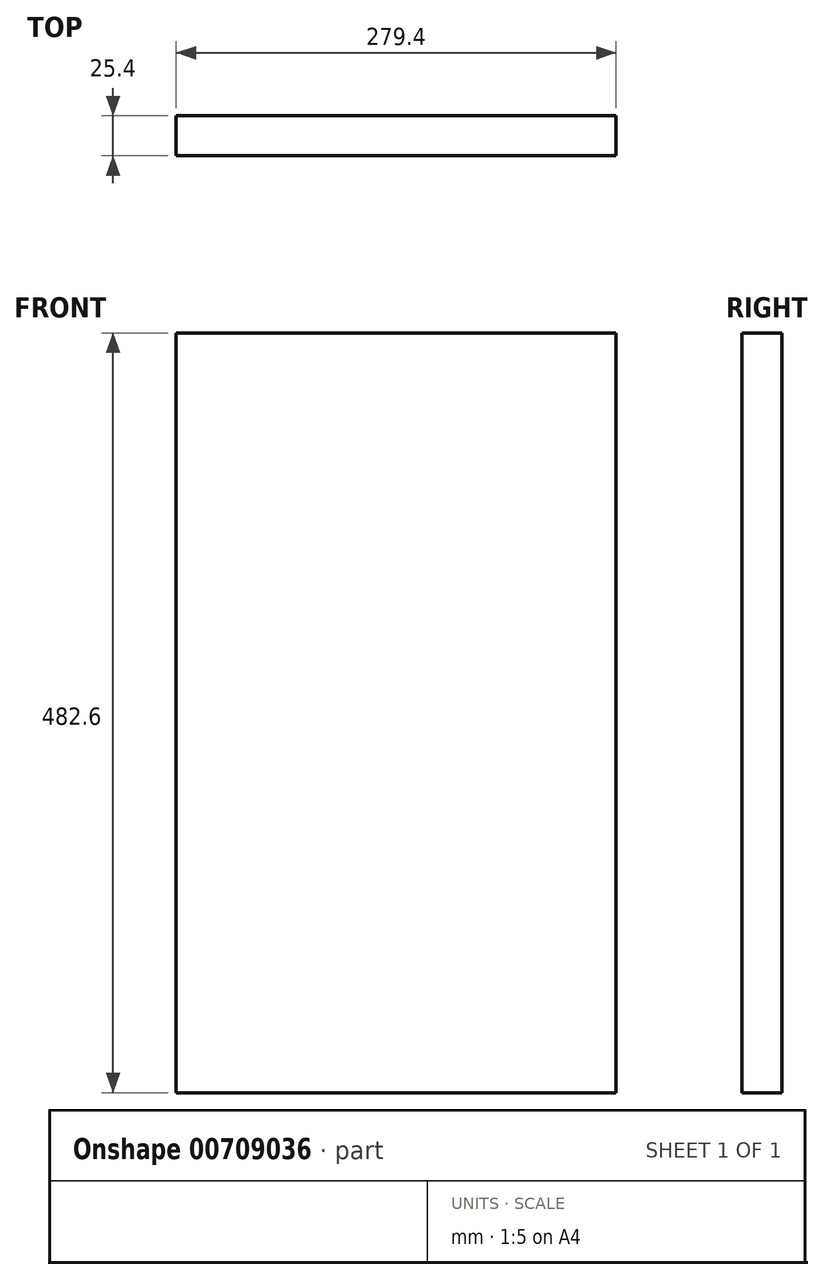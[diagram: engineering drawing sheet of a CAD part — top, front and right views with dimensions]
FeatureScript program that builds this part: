
annotation { "Feature Type Name" : "Feature", "Feature Type Description" : "" }
export const myFeature = defineFeature(function(context is Context, id is Id, definition is map)
    precondition{}
    {
        {
            var Q0;
            Q0=qCreatedBy(makeId("Front.planeOp"),FACE);
            var sketch = newSketch(context, id + "F0", { "sketchPlane" : qUnion([Q0])});
            skLineSegment(sketch, "E0.bottom", {"start": v(139.7, -241.3) * mm, "end": v(-139.7, -241.3) * mm});
            skLineSegment(sketch, "E0.top", {"start": v(139.7, 241.3) * mm, "end": v(-139.7, 241.3) * mm});
            skLineSegment(sketch, "E0.left", {"start": v(139.7, -241.3) * mm, "end": v(139.7, 241.3) * mm});
            skLineSegment(sketch, "E0.right", {"start": v(-139.7, -241.3) * mm, "end": v(-139.7, 241.3) * mm});
            skPoint(sketch, "E0.middle", {"position": v(0, 0) * mm});
            skSolve(sketch);
        }
        {
            var Q0;
            Q0 = qSketchRegion(id + "F0", true);
            extrude(context, id + "F1", {"entities" : qUnion([Q0]), "depth" : 25.4 * mm, "offsetDistance" : 25.4 * mm});
        }
    });
